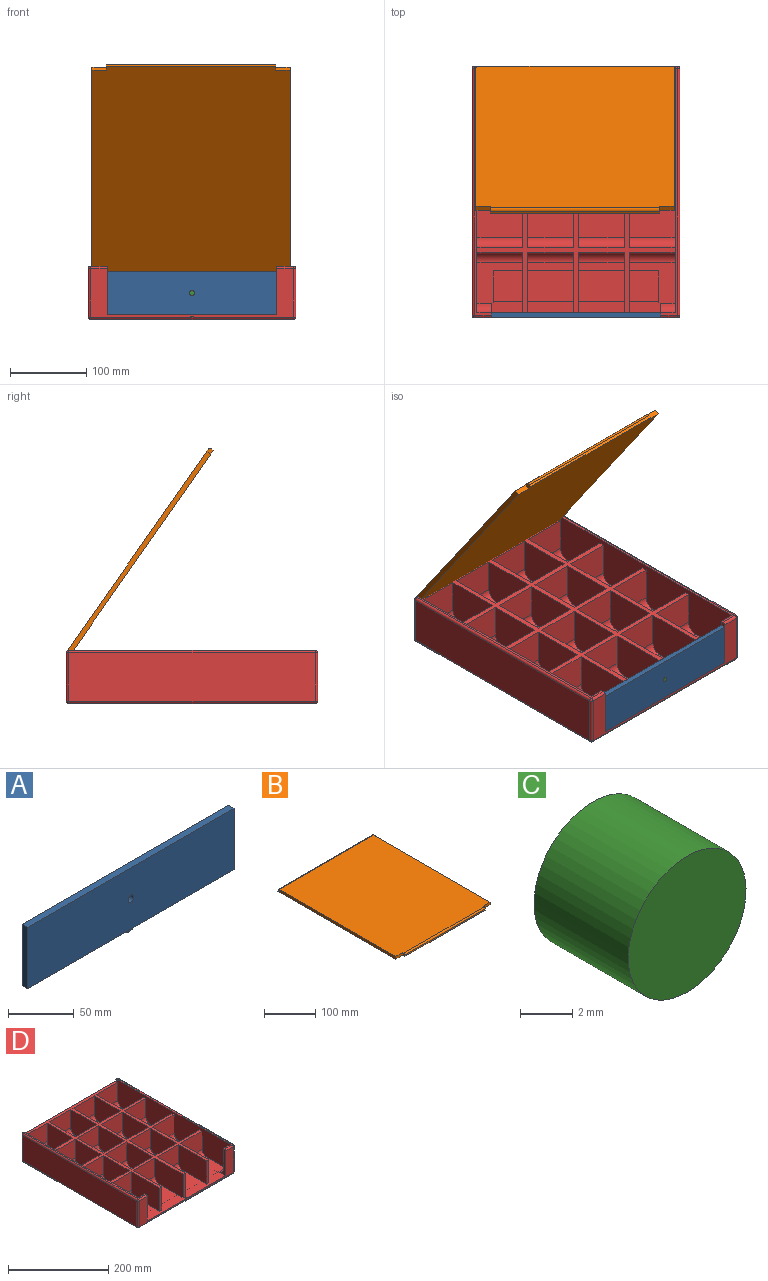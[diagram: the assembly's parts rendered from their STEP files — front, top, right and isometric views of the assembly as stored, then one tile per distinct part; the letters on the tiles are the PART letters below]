
ASSEMBLY  parts=4 mates=5
PART A: 13 faces, bbox 222.3x6.4x59.7 mm
  f0: plane 57.15x6.35mm, normal (-1,0,0), area 362.9mm2, adj f1,f3,f4,f5
  f1: plane 222.25x57.15mm, normal (0,-1,0), area 12669.9mm2, adj f0,f2,f4,f5,f11
  f2: plane 57.15x6.35mm, normal (1,0,0), area 362.9mm2, adj f1,f3,f4,f5
  f3: plane 222.25x57.15mm, normal (0,1,0), area 12701.6mm2, adj f0,f2,f4,f5
  f4: plane 222.25x6.35mm, normal (0,0,1), area 1411.3mm2, adj f0,f1,f2,f3
  f5: plane 222.25x6.35mm, normal (0,0,-1), area 1391.9mm2, adj f0,f1,f2,f3,f6,f7,f8,f9
  f6: plane 5.08x2.54mm, normal (0,-1,0), area 12.9mm2, adj f5,f7,f9,f10
  f7: plane 3.81x2.54mm, normal (-1,0,0), area 9.7mm2, adj f5,f6,f8,f10
  f8: plane 5.08x2.54mm, normal (0,1,0), area 12.9mm2, adj f5,f7,f9,f10
  f9: plane 3.81x2.54mm, normal (1,0,0), area 9.7mm2, adj f5,f6,f8,f10
  f10: plane 5.08x3.81mm, normal (0,0,-1), area 19.4mm2, adj f6,f7,f8,f9
  f11: cylinder r=3.17mm len=6.35mm, axis (0,-1,0), area 101.3mm2, adj f1,f12
  f12: plane 6.35x6.35mm, normal (0,-1,0), area 31.7mm2, adj f11
PART B: 16 faces, bbox 265.4x330.2x6.4 mm
  f0: plane 19.05x6.35mm, normal (0,-1,0), area 121mm2, adj f1,f7,f8,f9
  f1: plane 6.35x6.35mm, normal (-1,0,0), area 38.2mm2, adj f0,f2,f8,f9,f11
  f2: plane 222.25x3.18mm, normal (0,-1,0), area 705.6mm2, adj f1,f3,f9,f11
  f3: plane 6.35x6.35mm, normal (1,0,0), area 38.2mm2, adj f2,f4,f8,f9,f11
  f4: plane 19.05x6.35mm, normal (0,-1,0), area 121mm2, adj f3,f5,f8,f9
  f5: plane 323.85x6.35mm, normal (1,0,0), area 2049.2mm2, adj f4,f6,f8,f9,f10,f14
  f6: plane 260.35x3.18mm, normal (0,1,0), area 826.6mm2, adj f5,f7,f9,f10
  f7: plane 323.85x6.35mm, normal (-1,0,0), area 2049.2mm2, adj f0,f6,f8,f9,f10,f12
  f8: plane 323.85x260.35mm, normal (0,0,1), area 84193.4mm2, adj f0,f1,f3,f4,f5,f7,f10,f11
  f9: plane 330.2x260.35mm, normal (0,0,-1), area 85725.6mm2, adj f0,f1,f2,f3,f4,f5,f6,f7
  f10: cylinder r=3.17mm len=260.35mm, axis (1,0,0), area 1298.4mm2, adj f5,f6,f7,f8
  f11: cylinder r=3.17mm len=222.25mm, axis (-1,0,0), area 1108.4mm2, adj f1,f2,f3,f8
  f12: cylinder r=1.27mm len=2.54mm, axis (1,0,0), area 20.3mm2, adj f7,f13
  f13: plane 2.54x2.54mm, normal (-1,0,0), area 5.1mm2, adj f12
  f14: cylinder r=1.27mm len=2.54mm, axis (-1,0,0), area 20.3mm2, adj f5,f15
  f15: plane 2.54x2.54mm, normal (1,0,0), area 5.1mm2, adj f14
PART C: 3 faces, bbox 6.4x5.1x6.4 mm
  f0: cylinder r=3.17mm len=6.35mm, axis (0,1,0), area 101.3mm2, adj f1,f2
  f1: plane 6.35x6.35mm, normal (0,-1,0), area 31.7mm2, adj f0
  f2: plane 6.35x6.35mm, normal (0,1,0), area 31.7mm2, adj f0
PART D: 148 faces, bbox 273.1x330.2x69.9 mm
  f0: plane 60.33x47.63mm, normal (0,0,1), area 2873mm2, adj f64,f108,f109,f138
  f1: plane 60.33x47.63mm, normal (0,0,1), area 2873mm2, adj f64,f110,f111,f136
  f2: plane 60.33x47.63mm, normal (0,0,1), area 2873mm2, adj f64,f112,f114,f134
  f3: plane 60.33x44.45mm, normal (0,-1,0), area 2681.4mm2, adj f17,f92,f125,f135
  f4: plane 260.35x73.03mm, normal (0,0,1), area 16996.7mm2, adj f11,f28,f45,f53,f61,f64,f67,f68
  f5: plane 60.33x44.45mm, normal (0,1,0), area 2681.4mm2, adj f16,f92,f125,f135
  f6: plane 60.33x44.45mm, normal (0,-1,0), area 2681.4mm2, adj f15,f92,f127,f137
  f7: plane 60.33x44.45mm, normal (0,1,0), area 2681.4mm2, adj f14,f92,f127,f137
  f8: plane 60.33x44.45mm, normal (0,-1,0), area 2681.4mm2, adj f13,f92,f129,f139
  f9: plane 60.33x44.45mm, normal (0,1,0), area 2681.4mm2, adj f12,f92,f129,f139
  f10: plane 60.33x44.45mm, normal (0,-1,0), area 2681.4mm2, adj f11,f92,f132,f140
  f11: cylinder r=12.7mm len=60.33mm, axis (1,0,0), area 1203.4mm2, adj f4,f10,f132,f140
  f12: cylinder r=12.7mm len=60.33mm, axis (-1,0,0), area 1203.4mm2, adj f9,f18,f129,f139
  f13: cylinder r=12.7mm len=60.33mm, axis (1,0,0), area 1203.4mm2, adj f8,f18,f129,f139
  f14: cylinder r=12.7mm len=60.33mm, axis (-1,0,0), area 1203.4mm2, adj f7,f19,f127,f137
  f15: cylinder r=12.7mm len=60.33mm, axis (1,0,0), area 1203.4mm2, adj f6,f19,f127,f137
  f16: cylinder r=12.7mm len=60.33mm, axis (-1,0,0), area 1203.4mm2, adj f5,f20,f125,f135
  f17: cylinder r=12.7mm len=60.33mm, axis (-1,0,0), area 1203.4mm2, adj f3,f20,f125,f135
  f18: plane 60.33x47.63mm, normal (0,0,1), area 2873mm2, adj f12,f13,f129,f139
  f19: plane 60.33x47.63mm, normal (0,0,1), area 2873mm2, adj f14,f15,f127,f137
  f20: plane 60.33x47.63mm, normal (0,0,1), area 2873mm2, adj f16,f17,f125,f135
  f21: plane 60.33x44.45mm, normal (0,-1,0), area 2681.4mm2, adj f34,f92,f116,f126
  f22: plane 60.33x44.45mm, normal (0,1,0), area 2681.4mm2, adj f33,f92,f116,f126
  f23: plane 60.33x44.45mm, normal (0,-1,0), area 2681.4mm2, adj f32,f92,f118,f128
  f24: plane 60.33x44.45mm, normal (0,1,0), area 2681.4mm2, adj f31,f92,f118,f128
  f25: plane 60.33x44.45mm, normal (0,-1,0), area 2681.4mm2, adj f30,f92,f120,f130
  f26: plane 60.33x44.45mm, normal (0,1,0), area 2681.4mm2, adj f29,f92,f120,f130
  f27: plane 60.33x44.45mm, normal (0,-1,0), area 2681.4mm2, adj f28,f92,f122,f131
  f28: cylinder r=12.7mm len=60.33mm, axis (1,0,0), area 1203.4mm2, adj f4,f27,f122,f131
  f29: cylinder r=12.7mm len=60.33mm, axis (-1,0,0), area 1203.4mm2, adj f26,f35,f120,f130
  f30: cylinder r=12.7mm len=60.33mm, axis (1,0,0), area 1203.4mm2, adj f25,f35,f120,f130
  f31: cylinder r=12.7mm len=60.33mm, axis (-1,0,0), area 1203.4mm2, adj f24,f36,f118,f128
  f32: cylinder r=12.7mm len=60.33mm, axis (1,0,0), area 1203.4mm2, adj f23,f36,f118,f128
  f33: cylinder r=12.7mm len=60.33mm, axis (-1,0,0), area 1203.4mm2, adj f22,f37,f116,f126
  f34: cylinder r=12.7mm len=60.33mm, axis (-1,0,0), area 1203.4mm2, adj f21,f37,f116,f126
  f35: plane 60.33x47.63mm, normal (0,0,1), area 2873mm2, adj f29,f30,f120,f130
  f36: plane 60.33x47.63mm, normal (0,0,1), area 2873mm2, adj f31,f32,f118,f128
  f37: plane 60.33x47.63mm, normal (0,0,1), area 2873mm2, adj f33,f34,f116,f126
  f38: plane 60.33x44.45mm, normal (0,-1,0), area 2681.4mm2, adj f51,f53,f92,f117
  f39: plane 60.33x44.45mm, normal (0,1,0), area 2681.4mm2, adj f50,f53,f92,f117
  f40: plane 60.33x44.45mm, normal (0,-1,0), area 2681.4mm2, adj f49,f53,f92,f119
  f41: plane 60.33x44.45mm, normal (0,1,0), area 2681.4mm2, adj f48,f53,f92,f119
  f42: plane 60.33x44.45mm, normal (0,-1,0), area 2681.4mm2, adj f47,f53,f92,f121
  f43: plane 60.33x44.45mm, normal (0,1,0), area 2681.4mm2, adj f46,f53,f92,f121
  f44: plane 60.33x44.45mm, normal (0,-1,0), area 2681.4mm2, adj f45,f53,f92,f123
  f45: cylinder r=12.7mm len=60.33mm, axis (1,0,0), area 1203.4mm2, adj f4,f44,f53,f123
  f46: cylinder r=12.7mm len=60.33mm, axis (-1,0,0), area 1203.4mm2, adj f43,f52,f53,f121
  f47: cylinder r=12.7mm len=60.33mm, axis (1,0,0), area 1203.4mm2, adj f42,f52,f53,f121
  f48: cylinder r=12.7mm len=60.33mm, axis (-1,0,0), area 1203.4mm2, adj f41,f53,f54,f119
  f49: cylinder r=12.7mm len=60.33mm, axis (1,0,0), area 1203.4mm2, adj f40,f53,f54,f119
  f50: cylinder r=12.7mm len=60.33mm, axis (-1,0,0), area 1203.4mm2, adj f39,f53,f55,f117
  f51: cylinder r=12.7mm len=60.33mm, axis (-1,0,0), area 1203.4mm2, adj f38,f53,f55,f117
  f52: plane 60.33x47.63mm, normal (0,0,1), area 2873mm2, adj f46,f47,f53,f121
  f53: plane 323.85x63.5mm, normal (1,0,0), area 18828.7mm2, adj f4,f38,f39,f40,f41,f42,f43,f44
  f54: plane 60.33x47.63mm, normal (0,0,1), area 2873mm2, adj f48,f49,f53,f119
  f55: plane 60.33x47.63mm, normal (0,0,1), area 2873mm2, adj f50,f51,f53,f117
  f56: plane 323.85x22.23mm, normal (0,0,1), area 1088.7mm2, adj f64,f66,f68,f83,f86,f97
  f57: plane 266.7x63.5mm, normal (0,1,0), area 16108.8mm2, adj f53,f64,f71,f76,f81,f92,f97,f99
  f58: plane 323.85x22.23mm, normal (0,0,1), area 1088.7mm2, adj f53,f59,f67,f69,f70,f99
  f59: plane 50.8x19.05mm, normal (0,1,0), area 967.7mm2, adj f53,f58,f67,f113
  f60: plane 323.85x63.5mm, normal (-1,0,0), area 20564.5mm2, adj f69,f71,f74,f75
  f61: plane 266.7x63.5mm, normal (0,-1,0), area 3528.2mm2, adj f4,f67,f68,f70,f75,f80,f84,f86
  f62: plane 323.85x63.5mm, normal (1,0,0), area 20564.5mm2, adj f79,f81,f83,f84
  f63: plane 323.85x266.7mm, normal (0,0,-1), area 75403.1mm2, adj f74,f76,f79,f80,f143,f144,f146,f147
  f64: plane 323.85x63.5mm, normal (-1,0,0), area 18828.7mm2, adj f0,f1,f2,f4,f56,f57,f65,f66
  f65: plane 60.33x44.45mm, normal (0,-1,0), area 2681.4mm2, adj f64,f92,f114,f134
  f66: plane 50.8x19.05mm, normal (0,1,0), area 967.7mm2, adj f56,f64,f68,f115
  f67: plane 63.5x19.05mm, normal (1,0,0), area 435.7mm2, adj f4,f58,f59,f61,f70,f113
  f68: plane 63.5x19.05mm, normal (-1,0,0), area 435.7mm2, adj f4,f56,f61,f66,f86,f115
  f69: cylinder r=3.17mm len=323.85mm, axis (0,1,0), area 1615.1mm2, adj f58,f60,f72,f100
  f70: cylinder r=3.17mm len=22.23mm, axis (-1,0,0), area 110.8mm2, adj f58,f61,f67,f72
  f71: cylinder r=3.17mm len=63.5mm, axis (0,0,1), area 316.7mm2, adj f57,f60,f73,f100
  f72: sphere r=3.17mm, area 15.8mm2, adj f69,f70,f75
  f73: sphere r=3.17mm, area 15.8mm2, adj f71,f74,f76
  f74: cylinder r=3.17mm len=323.85mm, axis (0,-1,0), area 1615.1mm2, adj f60,f63,f73,f77
  f75: cylinder r=3.17mm len=63.5mm, axis (0,0,-1), area 316.7mm2, adj f60,f61,f72,f77
  f76: cylinder r=3.17mm len=266.7mm, axis (-1,0,0), area 1330.1mm2, adj f57,f63,f73,f78
  f77: sphere r=3.17mm, area 15.8mm2, adj f74,f75,f80
  f78: sphere r=3.17mm, area 15.8mm2, adj f76,f79,f81
  f79: cylinder r=3.17mm len=323.85mm, axis (0,1,0), area 1615.1mm2, adj f62,f63,f78,f82
  f80: cylinder r=3.17mm len=266.7mm, axis (1,0,0), area 1330.1mm2, adj f61,f63,f77,f82
  f81: cylinder r=3.17mm len=63.5mm, axis (0,0,-1), area 316.7mm2, adj f57,f62,f78,f98
  f82: sphere r=3.17mm, area 15.8mm2, adj f79,f80,f84
  f83: cylinder r=3.17mm len=323.85mm, axis (0,-1,0), area 1615.1mm2, adj f56,f62,f85,f98
  f84: cylinder r=3.17mm len=63.5mm, axis (0,0,1), area 316.7mm2, adj f61,f62,f82,f85
  f85: sphere r=3.17mm, area 15.8mm2, adj f83,f84,f86
  f86: cylinder r=3.17mm len=22.23mm, axis (-1,0,0), area 110.8mm2, adj f56,f61,f68,f85
  f87: plane 5.08x2.54mm, normal (0,-1,0), area 12.9mm2, adj f4,f88,f90,f91
  f88: plane 3.81x2.54mm, normal (1,0,0), area 9.7mm2, adj f4,f87,f89,f91
  f89: plane 5.08x2.54mm, normal (0,1,0), area 12.9mm2, adj f4,f88,f90,f91
  f90: plane 3.81x2.54mm, normal (-1,0,0), area 9.7mm2, adj f4,f87,f89,f91
  f91: plane 5.08x3.81mm, normal (0,0,1), area 19.4mm2, adj f87,f88,f89,f90
  f92: plane 323.85x260.35mm, normal (0,0,1), area 12298.4mm2, adj f3,f5,f6,f7,f8,f9,f10,f21
  f93: cylinder r=1.27mm len=2.54mm, axis (1,0,0), area 20.3mm2, adj f53,f94
  f94: plane 2.54x2.54mm, normal (1,0,0), area 5.1mm2, adj f93
  f95: cylinder r=1.27mm len=2.54mm, axis (-1,0,0), area 20.3mm2, adj f64,f96
  f96: plane 2.54x2.54mm, normal (-1,0,0), area 5.1mm2, adj f95
  f97: cylinder r=3.17mm len=3.18mm, axis (1,0,0), area 15.8mm2, adj f56,f57,f64,f98
  f98: sphere r=3.17mm, area 15.8mm2, adj f81,f83,f97
  f99: cylinder r=3.17mm len=3.18mm, axis (1,0,0), area 15.8mm2, adj f53,f57,f58,f100
  f100: sphere r=3.17mm, area 15.8mm2, adj f69,f71,f99
  f101: plane 60.33x44.45mm, normal (0,1,0), area 2681.4mm2, adj f64,f92,f112,f134
  f102: plane 60.33x44.45mm, normal (0,-1,0), area 2681.4mm2, adj f64,f92,f111,f136
  f103: plane 60.33x44.45mm, normal (0,1,0), area 2681.4mm2, adj f64,f92,f110,f136
  f104: plane 60.33x44.45mm, normal (0,-1,0), area 2681.4mm2, adj f64,f92,f109,f138
  f105: plane 60.33x44.45mm, normal (0,1,0), area 2681.4mm2, adj f64,f92,f108,f138
  f106: plane 60.33x44.45mm, normal (0,-1,0), area 2681.4mm2, adj f64,f92,f107,f141
  f107: cylinder r=12.7mm len=60.33mm, axis (1,0,0), area 1203.4mm2, adj f4,f64,f106,f141
  f108: cylinder r=12.7mm len=60.33mm, axis (-1,0,0), area 1203.4mm2, adj f0,f64,f105,f138
  f109: cylinder r=12.7mm len=60.33mm, axis (1,0,0), area 1203.4mm2, adj f0,f64,f104,f138
  f110: cylinder r=12.7mm len=60.33mm, axis (-1,0,0), area 1203.4mm2, adj f1,f64,f103,f136
  f111: cylinder r=12.7mm len=60.33mm, axis (1,0,0), area 1203.4mm2, adj f1,f64,f102,f136
  f112: cylinder r=12.7mm len=60.33mm, axis (-1,0,0), area 1203.4mm2, adj f2,f64,f101,f134
  f113: cylinder r=12.7mm len=19.05mm, axis (1,0,0), area 380mm2, adj f4,f53,f59,f67
  f114: cylinder r=12.7mm len=60.33mm, axis (-1,0,0), area 1203.4mm2, adj f2,f64,f65,f134
  f115: cylinder r=12.7mm len=19.05mm, axis (1,0,0), area 380mm2, adj f4,f64,f66,f68
  f116: plane 73.03x57.15mm, normal (1,0,0), area 4104.2mm2, adj f21,f22,f33,f34,f37,f92
  f117: plane 73.03x57.15mm, normal (-1,0,0), area 4104.2mm2, adj f38,f39,f50,f51,f55,f92
  f118: plane 73.03x57.15mm, normal (1,0,0), area 4104.2mm2, adj f23,f24,f31,f32,f36,f92
  f119: plane 73.03x57.15mm, normal (-1,0,0), area 4104.2mm2, adj f40,f41,f48,f49,f54,f92
  f120: plane 73.03x57.15mm, normal (1,0,0), area 4104.2mm2, adj f25,f26,f29,f30,f35,f92
  f121: plane 73.03x57.15mm, normal (-1,0,0), area 4104.2mm2, adj f42,f43,f46,f47,f52,f92
  f122: plane 79.38x57.15mm, normal (1,0,0), area 4501.7mm2, adj f4,f27,f28,f92,f124
  f123: plane 79.38x57.15mm, normal (-1,0,0), area 4501.7mm2, adj f4,f44,f45,f92,f124
  f124: plane 57.15x6.35mm, normal (0,-1,0), area 362.9mm2, adj f4,f92,f122,f123
  f125: plane 73.03x57.15mm, normal (1,0,0), area 4104.2mm2, adj f3,f5,f16,f17,f20,f92
  f126: plane 73.03x57.15mm, normal (-1,0,0), area 4104.2mm2, adj f21,f22,f33,f34,f37,f92
  f127: plane 73.03x57.15mm, normal (1,0,0), area 4104.2mm2, adj f6,f7,f14,f15,f19,f92
  f128: plane 73.03x57.15mm, normal (-1,0,0), area 4104.2mm2, adj f23,f24,f31,f32,f36,f92
  f129: plane 73.03x57.15mm, normal (1,0,0), area 4104.2mm2, adj f8,f9,f12,f13,f18,f92
  f130: plane 73.03x57.15mm, normal (-1,0,0), area 4104.2mm2, adj f25,f26,f29,f30,f35,f92
  f131: plane 79.38x57.15mm, normal (-1,0,0), area 4501.7mm2, adj f4,f27,f28,f92,f133
  f132: plane 79.38x57.15mm, normal (1,0,0), area 4501.7mm2, adj f4,f10,f11,f92,f133
  f133: plane 57.15x6.35mm, normal (0,-1,0), area 362.9mm2, adj f4,f92,f131,f132
  f134: plane 73.03x57.15mm, normal (1,0,0), area 4104.2mm2, adj f2,f65,f92,f101,f112,f114
  f135: plane 73.03x57.15mm, normal (-1,0,0), area 4104.2mm2, adj f3,f5,f16,f17,f20,f92
  f136: plane 73.03x57.15mm, normal (1,0,0), area 4104.2mm2, adj f1,f92,f102,f103,f110,f111
  f137: plane 73.03x57.15mm, normal (-1,0,0), area 4104.2mm2, adj f6,f7,f14,f15,f19,f92
  f138: plane 73.03x57.15mm, normal (1,0,0), area 4104.2mm2, adj f0,f92,f104,f105,f108,f109
  f139: plane 73.03x57.15mm, normal (-1,0,0), area 4104.2mm2, adj f8,f9,f12,f13,f18,f92
  f140: plane 79.38x57.15mm, normal (-1,0,0), area 4501.7mm2, adj f4,f10,f11,f92,f142
  f141: plane 79.38x57.15mm, normal (1,0,0), area 4501.7mm2, adj f4,f92,f106,f107,f142
  f142: plane 57.15x6.35mm, normal (0,-1,0), area 362.9mm2, adj f4,f92,f140,f141
  f143: plane 50.8x5.08mm, normal (1,0,0), area 239.6mm2, adj f63,f145,f146,f147
  f144: plane 50.8x5.08mm, normal (-1,0,0), area 239.6mm2, adj f63,f145,f146,f147
  f145: plane 215.9x40.64mm, normal (0,0,-1), area 8774.2mm2, adj f143,f144,f146,f147
  f146: cylinder r=5.08mm len=215.9mm, axis (1,0,0), area 1722.8mm2, adj f63,f143,f144,f145
  f147: plane 215.9x5.08mm, normal (0,-0.71,-0.71), area 1551.1mm2, adj f63,f143,f144,f145
PLACE A t=(218.37,-89.78,49.73)mm
PLACE B rot(axis=(-1,0,0),55deg) t=(-143.04,15.48,370.91)mm
PLACE C t=(-11.6,-119.94,78.3)mm
PLACE D t=(230.01,-125.02,43.38)mm
MATE slider C.f0 <-> A.f11  axis (0,-1,0) through (-11.6,-125.02,78.3)mm
MATE planar D.f67 <-> A.f0  axis (1,0,0) through (-122.72,-121.35,79.03)mm
MATE pin_slot A.f10 <-> D.f91  axis (0,0,-1) through (-11.6,-121.84,47.19)mm
MATE planar C.f0 <-> A.f11  axis (0,-1,0) through (-11.6,-125.02,78.3)mm
MATE revolute B.f10 <-> D.f97  axis (1,0,0) through (119.85,202.01,110.05)mm
